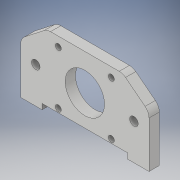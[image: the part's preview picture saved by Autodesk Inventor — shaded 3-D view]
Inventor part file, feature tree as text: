
AUTODESK INVENTOR PART (.ipt)
format: ipt  version: 2019 (Build 230136000, 136)  size: 154,624 bytes
history: native  units: mm
features: extrude x1, fillet x1, sketch x1
ambient origin geometry x8: Origin, YZ Plane, XZ Plane, XY Plane, X Axis, Y Axis, Z Axis, Center Point
bodies: Body1 (feature_tree)
feature tree (3):
  extrude  "Extrusion2"  Depth=42.0mm
  fillet  "Fillet2"  Radius=22.340214mm
  sketch  "Sketch1"  dims[d0=30.0mm d1=30.0mm d3=22.340214mm d4=75.0mm d5=5.0mm d7=5.0mm d9=28.678mm d10=28.678mm d13=3.5mm d14=3.5mm d15=15.5mm d16=15.5mm d21=3.5mm d22=3.5mm d23=31.0mm d24=23.0mm d25=6.0mm d26=0.0mm d27=6.0mm d28=50.0mm d29=12.5mm d30=3.2mm d31=17.8mm d32=2.3mm d33=22.340214mm d34=44.281401mm d35=12.0mm d36=12.0mm d37=42.0mm]
